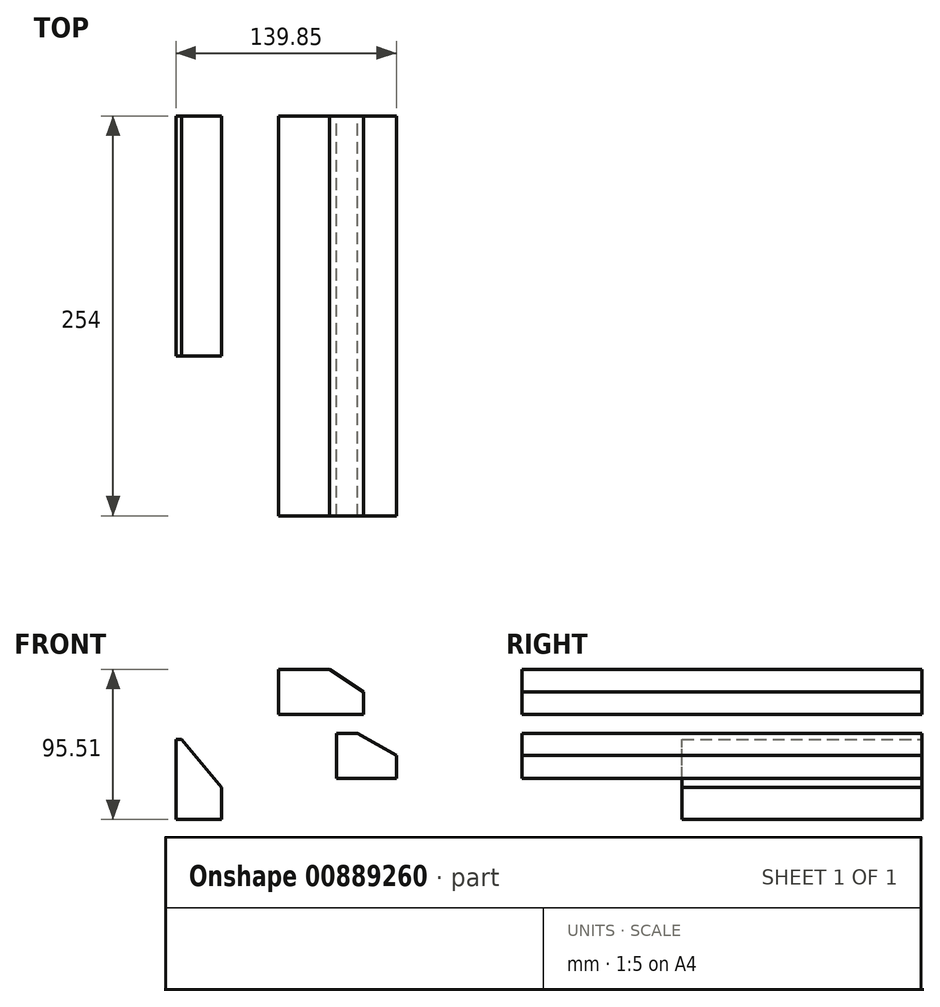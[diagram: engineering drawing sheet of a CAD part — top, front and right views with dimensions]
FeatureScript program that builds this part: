
annotation { "Feature Type Name" : "Feature", "Feature Type Description" : "" }
export const myFeature = defineFeature(function(context is Context, id is Id, definition is map)
    precondition{}
    {
        {
            var Q0;
            Q0=qCreatedBy(makeId("Front.planeOp"),FACE);
            var sketch = newSketch(context, id + "F0", { "sketchPlane" : qUnion([Q0])});
            skLineSegment(sketch, "E0.bottom", {"start": v(0, 0) * mm, "end": v(38.1, 0) * mm});
            skLineSegment(sketch, "E0.top", {"start": v(0, 28.83) * mm, "end": v(13.33, 28.83) * mm});
            skLineSegment(sketch, "E0.left", {"start": v(0, 0) * mm, "end": v(0, 28.83) * mm});
            skLineSegment(sketch, "E0.right", {"start": v(38.1, 0) * mm, "end": v(38.1, 14.6) * mm});
            skLineSegment(sketch, "E1", {"start": v(38.1, 14.6) * mm, "end": v(13.33, 28.83) * mm});
            skSolve(sketch);
        }
        {
            var Q0;
            Q0=makeQuery(id+"F0.imprint","IMPRINT",FACE,{"disambiguationData":[TD([[makeQuery(id+"F0.imprint","IMPRINT",EDGE,{"derivedFrom":sQuery(id+"F0.wireOp",EDGE,"E0.bottom")}),1.0]])]});
            extrude(context, id + "F1", {"entities" : qUnion([Q0]), "depth" : 254 * mm, "offsetDistance" : 25.4 * mm});
        }
        {
            var Q0;
            Q0=qCreatedBy(makeId("Front.planeOp"),FACE);
            var sketch = newSketch(context, id + "F2", { "sketchPlane" : qUnion([Q0])});
            skLineSegment(sketch, "E2.bottom", {"start": v(-36.62, 69.47) * mm, "end": v(-4.23, 69.47) * mm});
            skLineSegment(sketch, "E2.top", {"start": v(-36.62, 40.64) * mm, "end": v(17.36, 40.64) * mm});
            skLineSegment(sketch, "E2.left", {"start": v(-36.62, 69.47) * mm, "end": v(-36.62, 40.64) * mm});
            skLineSegment(sketch, "E2.right", {"start": v(17.36, 55.06) * mm, "end": v(17.36, 40.64) * mm});
            skLineSegment(sketch, "E3", {"start": v(-4.23, 69.47) * mm, "end": v(17.36, 55.06) * mm});
            skPoint(sketch, "E4.orphan", {"position": v(17.36, 69.47) * mm});
            skSolve(sketch);
        }
        {
            var Q0;
            Q0=makeQuery(id+"F2.imprint","IMPRINT",FACE,{"disambiguationData":[TD([[makeQuery(id+"F2.imprint","IMPRINT",EDGE,{"derivedFrom":sQuery(id+"F2.wireOp",EDGE,"E2.bottom")}),-1.0]])]});
            extrude(context, id + "F3", {"entities" : qUnion([Q0]), "depth" : 254 * mm, "offsetDistance" : 25.4 * mm});
        }
        {
            var Q0;
            Q0=qCreatedBy(makeId("Front.planeOp"),FACE);
            var sketch = newSketch(context, id + "F4", { "sketchPlane" : qUnion([Q0])});
            skLineSegment(sketch, "E5.bottom", {"start": v(-101.75, -26.04) * mm, "end": v(-72.92, -26.04) * mm});
            skLineSegment(sketch, "E5.top", {"start": v(-101.75, 24.87) * mm, "end": v(-72.92, 24.87) * mm});
            skLineSegment(sketch, "E5.left", {"start": v(-101.75, -26.04) * mm, "end": v(-101.75, 24.87) * mm});
            skLineSegment(sketch, "E5.right", {"start": v(-72.92, -26.04) * mm, "end": v(-72.92, 24.87) * mm});
            skSolve(sketch);
        }
        {
            var Q0;
            Q0=makeQuery(id+"F4.imprint","IMPRINT",FACE,{"disambiguationData":[TD([[makeQuery(id+"F4.imprint","IMPRINT",EDGE,{"derivedFrom":sQuery(id+"F4.wireOp",EDGE,"E5.bottom")}),1.0]])]});
            extrude(context, id + "F5", {"entities" : qUnion([Q0]), "depth" : 152.4 * mm, "offsetDistance" : 25.4 * mm});
        }
        {
            var Q0;
            Q0=makeQuery(id+"F5.opExtrude","SWEPT_EDGE",EDGE,{"disambiguationData":[OSD([sQuery(id+"F4.wireOp",EDGE,"E5.top"),sQuery(id+"F4.wireOp",EDGE,"E5.right")])]});
            chamfer(context, id + "F6", {"entities" : qUnion([Q0]), "chamferType" : ChamferType.TWO_OFFSETS, "width1" : 25.4 * mm, "oppositeDirection" : false, "width2" : 30.48 * mm, "tangentPropagation" : true});
        }
    });
